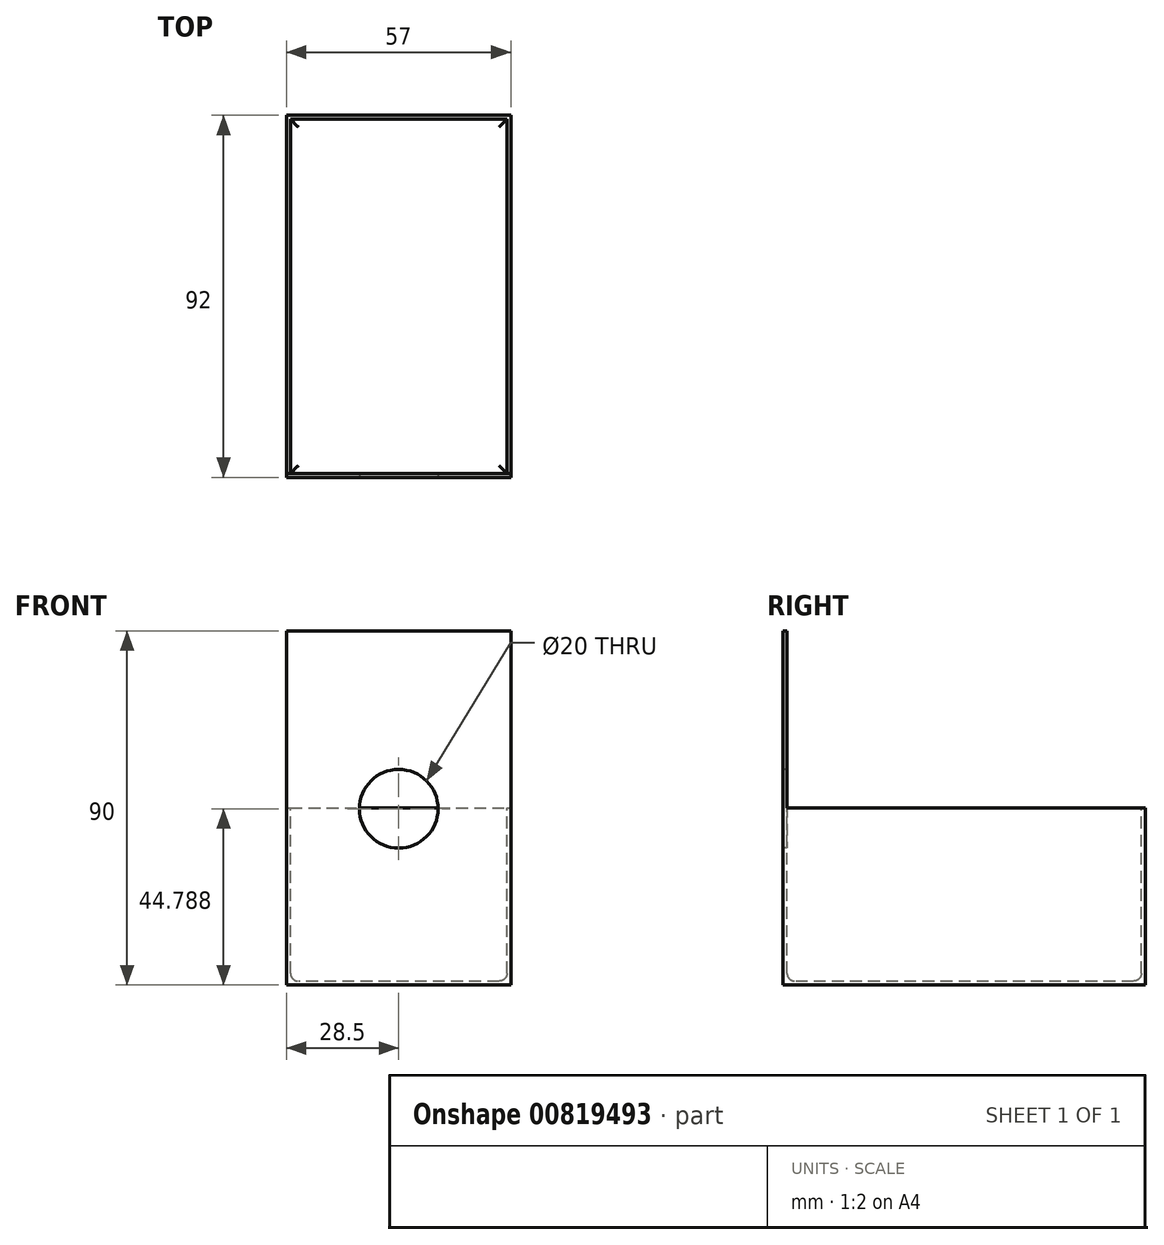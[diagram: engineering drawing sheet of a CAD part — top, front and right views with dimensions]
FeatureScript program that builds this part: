
annotation { "Feature Type Name" : "Feature", "Feature Type Description" : "" }
export const myFeature = defineFeature(function(context is Context, id is Id, definition is map)
    precondition{}
    {
        {
            var Q0;
            Q0=qCreatedBy(makeId("Top.planeOp"),FACE);
            var sketch = newSketch(context, id + "F0", { "sketchPlane" : qUnion([Q0])});
            skLineSegment(sketch, "E0.bottom", {"start": v(28.5, 46) * mm, "end": v(-28.5, 46) * mm});
            skLineSegment(sketch, "E0.top", {"start": v(28.5, -46) * mm, "end": v(-28.5, -46) * mm});
            skLineSegment(sketch, "E0.left", {"start": v(28.5, 46) * mm, "end": v(28.5, -46) * mm});
            skLineSegment(sketch, "E0.right", {"start": v(-28.5, 46) * mm, "end": v(-28.5, -46) * mm});
            skPoint(sketch, "E0.middle", {"position": v(0, 0) * mm});
            skSolve(sketch);
        }
        {
            var Q0;
            Q0=makeQuery(id+"F0.imprint","IMPRINT",FACE,{"disambiguationData":[TD([[makeQuery(id+"F0.imprint","IMPRINT",EDGE,{"derivedFrom":sQuery(id+"F0.wireOp",EDGE,"E0.bottom")}),1.0]])]});
            extrude(context, id + "F1", {"entities" : qUnion([Q0]), "depth" : 90 * mm, "offsetDistance" : 25 * mm});
        }
        {
            var Q0;
            Q0=makeQuery(id+"F1.opExtrude","CAP_FACE",FACE,{"disambiguationData":[OSD([sQuery(id+"F0.wireOp",EDGE,"E0.bottom"),sQuery(id+"F0.wireOp",EDGE,"E0.top"),sQuery(id+"F0.wireOp",EDGE,"E0.left"),sQuery(id+"F0.wireOp",EDGE,"E0.right")])],"isStart":false});
            var sketch = newSketch(context, id + "F2", { "sketchPlane" : qUnion([Q0])});
            skLineSegment(sketch, "E1.bottom", {"start": v(27.5, 45) * mm, "end": v(-27.5, 45) * mm});
            skLineSegment(sketch, "E1.top", {"start": v(27.5, -45) * mm, "end": v(-27.5, -45) * mm});
            skLineSegment(sketch, "E1.left", {"start": v(27.5, 45) * mm, "end": v(27.5, -45) * mm});
            skLineSegment(sketch, "E1.right", {"start": v(-27.5, 45) * mm, "end": v(-27.5, -45) * mm});
            skPoint(sketch, "E1.middle", {"position": v(0, 0) * mm});
            skSolve(sketch);
        }
        {
            var Q0;
            Q0=makeQuery(id+"F2.imprint","IMPRINT",FACE,{"disambiguationData":[TD([[makeQuery(id+"F2.imprint","IMPRINT",EDGE,{"derivedFrom":sQuery(id+"F2.wireOp",EDGE,"E1.bottom")}),1.0]])]});
            extrude(context, id + "F3", {"entities" : qUnion([Q0]), "operationType" : NewBodyOperationType.REMOVE, "oppositeDirection" : true, "depth" : 89 * mm, "offsetDistance" : 25 * mm});
        }
        {
            var Q0;
            Q0=makeQuery(id+"F1.opExtrude","CAP_FACE",FACE,{"disambiguationData":[OSD([sQuery(id+"F0.wireOp",EDGE,"E0.bottom"),sQuery(id+"F0.wireOp",EDGE,"E0.top"),sQuery(id+"F0.wireOp",EDGE,"E0.left"),sQuery(id+"F0.wireOp",EDGE,"E0.right")])],"isStart":false});
            var sketch = newSketch(context, id + "F4", { "sketchPlane" : qUnion([Q0])});
            skLineSegment(sketch, "E2.bottom", {"start": v(-28.5, 46) * mm, "end": v(28.5, 46) * mm});
            skLineSegment(sketch, "E2.top", {"start": v(-28.5, -45) * mm, "end": v(28.5, -45) * mm});
            skLineSegment(sketch, "E2.left", {"start": v(-28.5, 46) * mm, "end": v(-28.5, -45) * mm});
            skLineSegment(sketch, "E2.right", {"start": v(28.5, 46) * mm, "end": v(28.5, -45) * mm});
            skSolve(sketch);
        }
        {
            var Q0;
            Q0 = qSketchRegion(id + "F4", true);
            extrude(context, id + "F5", {"entities" : qUnion([Q0]), "operationType" : NewBodyOperationType.REMOVE, "oppositeDirection" : true, "depth" : 45 * mm, "offsetDistance" : 25 * mm});
        }
        {
            var Q0;
            Q0=makeQuery(id+"F1.opExtrude","SWEPT_FACE",FACE,{"disambiguationData":[OSD([sQuery(id+"F0.wireOp",EDGE,"E0.top")])]});
            var sketch = newSketch(context, id + "F6", { "sketchPlane" : qUnion([Q0])});
            skCircle(sketch, "E3", {"center": v(0, 44.79) * mm, "radius": 10 * mm});
            skSolve(sketch);
        }
        {
            var Q0;
            Q0 = qSketchRegion(id + "F6", true);
            extrude(context, id + "F7", {"entities" : qUnion([Q0]), "operationType" : NewBodyOperationType.REMOVE, "oppositeDirection" : true, "depth" : 1 * mm, "offsetDistance" : 25 * mm});
        }
        {
            var Q0;
            Q0=makeQuery(id+"F3.boolean.opBoolean","COPY",FACE,{"derivedFrom":makeQuery(id+"F3.opExtrude","CAP_FACE",FACE,{"disambiguationData":[OSD([sQuery(id+"F2.wireOp",EDGE,"E1.bottom"),sQuery(id+"F2.wireOp",EDGE,"E1.top"),sQuery(id+"F2.wireOp",EDGE,"E1.left"),sQuery(id+"F2.wireOp",EDGE,"E1.right")])],"isStart":false})});
            fillet(context, id + "F8", {"entities" : qUnion([Q0]), "radius" : 2 * mm, "tangentPropagation" : true, "allowEdgeOverflow" : false});
        }
    });
